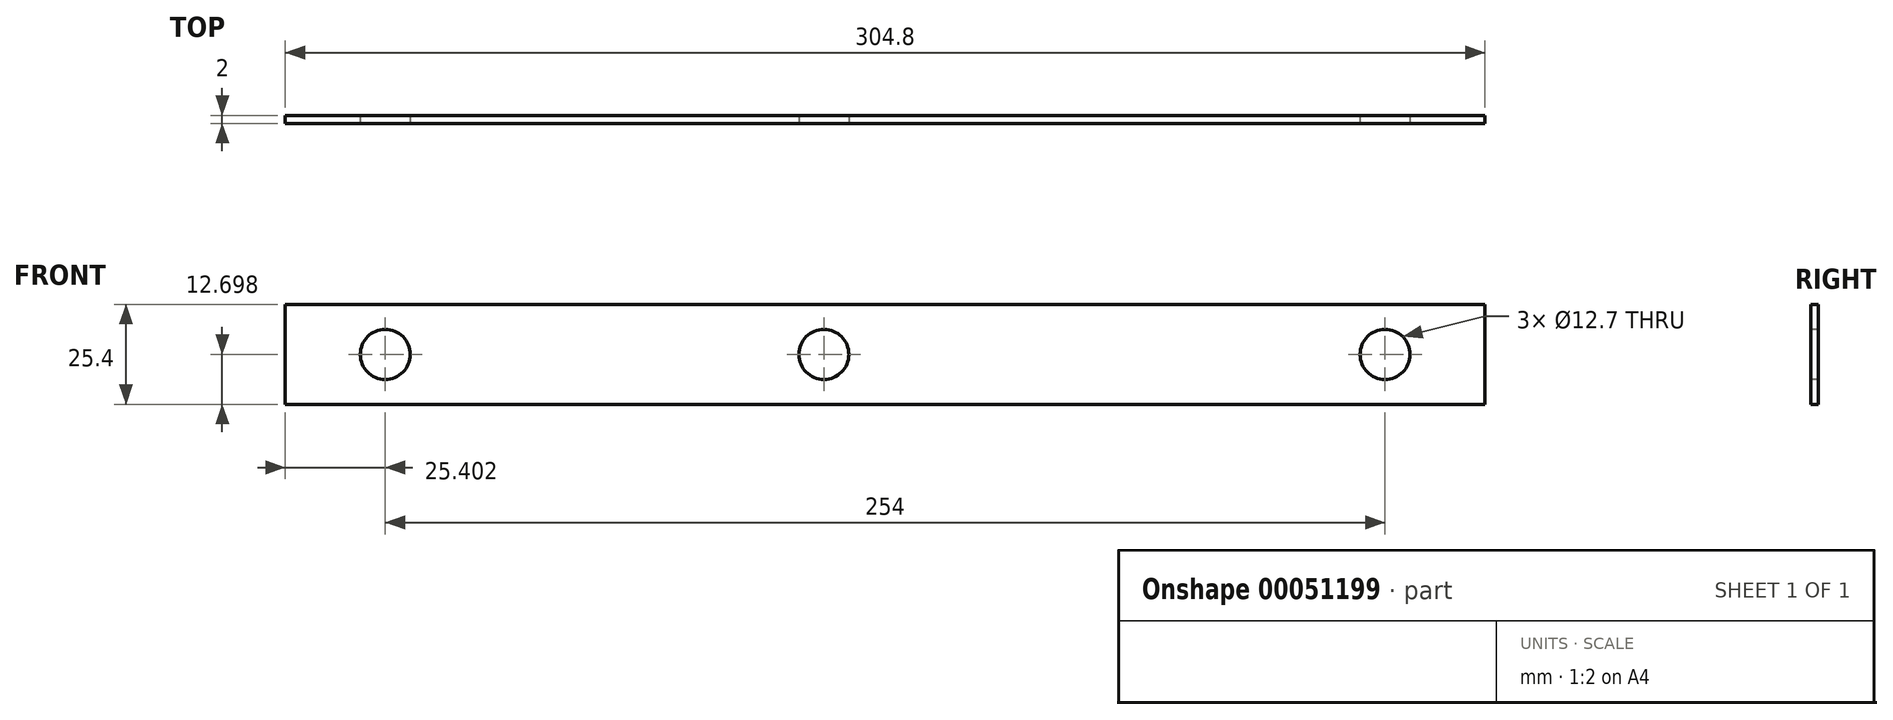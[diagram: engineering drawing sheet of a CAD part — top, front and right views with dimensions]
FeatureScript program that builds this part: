
annotation { "Feature Type Name" : "Feature", "Feature Type Description" : "" }
export const myFeature = defineFeature(function(context is Context, id is Id, definition is map)
    precondition{}
    {
        {
            var Q0;
            Q0=qCreatedBy(makeId("Front.planeOp"),FACE);
            var sketch = newSketch(context, id + "F0", { "sketchPlane" : qUnion([Q0])});
            skLineSegment(sketch, "E0.bottom", {"start": v(-346, 23.66) * mm, "end": v(-41.2, 23.66) * mm});
            skLineSegment(sketch, "E0.top", {"start": v(-346, -1.74) * mm, "end": v(-41.2, -1.74) * mm});
            skLineSegment(sketch, "E0.left", {"start": v(-346, 23.66) * mm, "end": v(-346, -1.74) * mm});
            skLineSegment(sketch, "E0.right", {"start": v(-41.2, 23.66) * mm, "end": v(-41.2, -1.74) * mm});
            skSolve(sketch);
        }
        {
            var Q0;
            Q0=makeQuery(id+"F0.imprint","IMPRINT",FACE,{"disambiguationData":[TD([[makeQuery(id+"F0.imprint","IMPRINT",EDGE,{"derivedFrom":sQuery(id+"F0.wireOp",EDGE,"E0.bottom")}),-1.0]])]});
            var sketch = newSketch(context, id + "F1", { "sketchPlane" : qUnion([Q0])});
            skCircle(sketch, "E1", {"center": v(-209.17, 10.96) * mm, "radius": 6.35 * mm});
            skSolve(sketch);
        }
        {
            var Q0;
            Q0 = qSketchRegion(id + "F0", true);
            extrude(context, id + "F2", {"entities" : qUnion([Q0]), "oppositeDirection" : true, "depth" : 2 * mm});
        }
        {
            var Q0;
            Q0=makeQuery(id+"F1.imprint","IMPRINT",FACE,{"disambiguationData":[TD([[makeQuery(id+"F1.imprint","IMPRINT",EDGE,{"derivedFrom":sQuery(id+"F1.wireOp",EDGE,"E1")}),1.0]])]});
            var Q1;
            Q1=sQuery(id+"F1.wireOp",EDGE,"E1");
            extrude(context, id + "F3", {"entities" : qUnion([Q0]), "operationType" : NewBodyOperationType.REMOVE, "surfaceEntities" : qUnion([Q1]), "oppositeDirection" : true, "depth" : 108 * mm});
        }
        {
            var Q0;
            Q0=makeQuery(id+"F2.opExtrude","CAP_FACE",FACE,{"disambiguationData":[OSD([sQuery(id+"F0.wireOp",EDGE,"E0.bottom"),sQuery(id+"F0.wireOp",EDGE,"E0.top"),sQuery(id+"F0.wireOp",EDGE,"E0.left"),sQuery(id+"F0.wireOp",EDGE,"E0.right")])],"isStart":true});
            var sketch = newSketch(context, id + "F4", { "sketchPlane" : qUnion([Q0])});
            skCircle(sketch, "E2", {"center": v(-320.6, 10.96) * mm, "radius": 6.35 * mm});
            skCircle(sketch, "E3", {"center": v(-66.6, 10.96) * mm, "radius": 6.35 * mm});
            skSolve(sketch);
        }
        {
            var Q0;
            Q0 = qSketchRegion(id + "F4", true);
            extrude(context, id + "F5", {"entities" : qUnion([Q0]), "operationType" : NewBodyOperationType.REMOVE, "oppositeDirection" : true, "depth" : 25.4 * mm});
        }
    });
